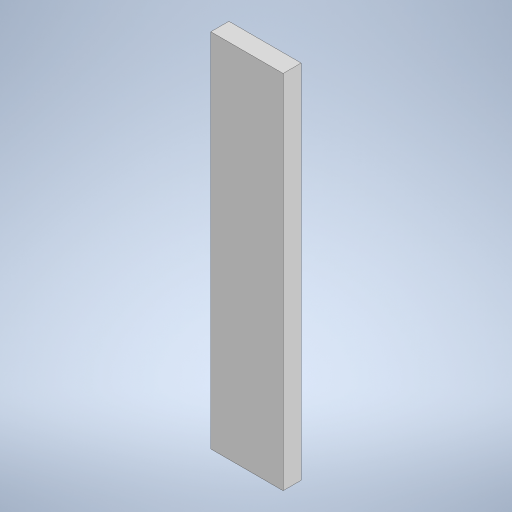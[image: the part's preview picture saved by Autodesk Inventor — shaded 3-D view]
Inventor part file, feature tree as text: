
AUTODESK INVENTOR PART (.ipt)
format: ipt  version: 2024.3 (Build 283343000, 343)  size: 206,848 bytes
history: native  units: mm
features: extrude x1, sketch x1
ambient origin geometry x8: Origin, YZ Plane, XZ Plane, XY Plane, X Axis, Y Axis, Z Axis, Center Point
bodies: Solido1 (feature_tree)
feature tree (2):
  extrude  "Estrusione1"  Depth=0.4mm
  sketch  "Schizzo1"
